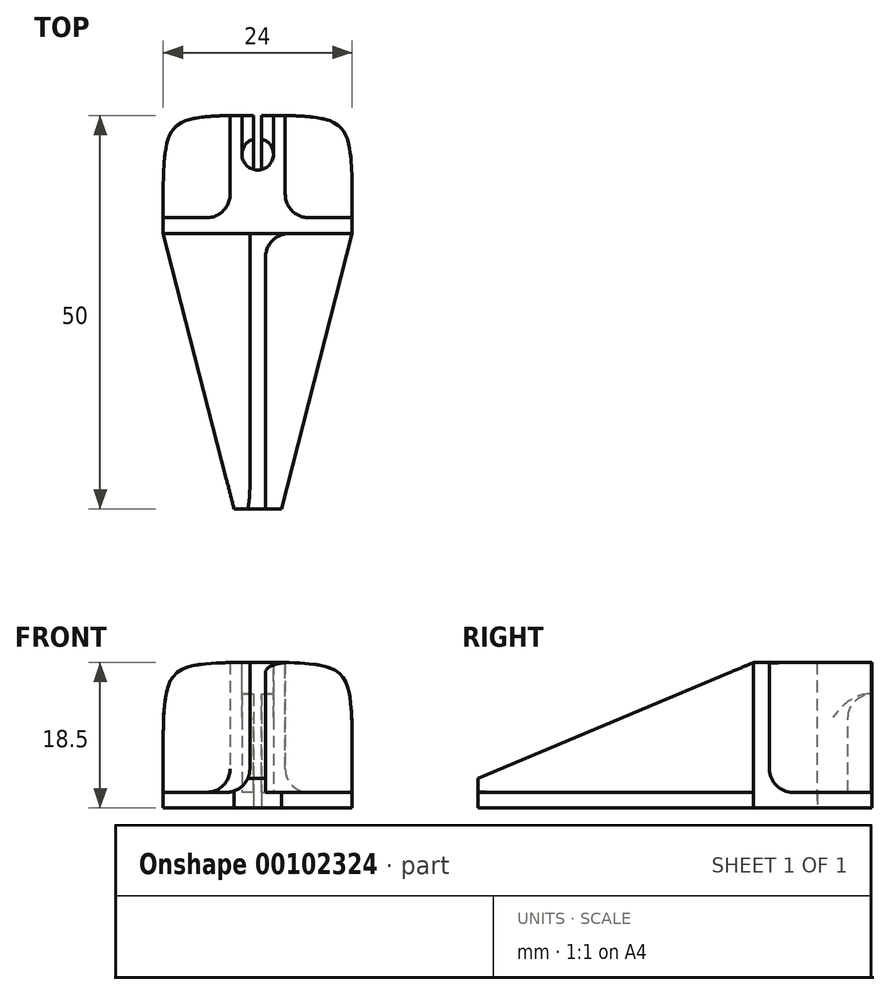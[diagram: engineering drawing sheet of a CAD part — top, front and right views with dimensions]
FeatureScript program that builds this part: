
annotation { "Feature Type Name" : "Feature", "Feature Type Description" : "" }
export const myFeature = defineFeature(function(context is Context, id is Id, definition is map)
    precondition{}
    {
        {
            var Q0;
            Q0=qCreatedBy(makeId("Top.planeOp"),FACE);
            var sketch = newSketch(context, id + "F0", { "sketchPlane" : qUnion([Q0])});
            skLineSegment(sketch, "E0", {"start": v(0.5, 1.94) * mm, "end": v(0.5, 4.94) * mm});
            skLineSegment(sketch, "E1", {"start": v(0.5, 4.94) * mm, "end": v(12, 4.94) * mm});
            skLineSegment(sketch, "E2", {"start": v(12, 4.94) * mm, "end": v(12, -10.06) * mm});
            skLineSegment(sketch, "E3", {"start": v(12, -10.06) * mm, "end": v(3, -45.06) * mm});
            skLineSegment(sketch, "E4", {"start": v(3, -45.06) * mm, "end": v(-3, -45.06) * mm});
            skLineSegment(sketch, "E5", {"start": v(-3, -45.06) * mm, "end": v(-12, -10.06) * mm});
            skLineSegment(sketch, "E6", {"start": v(-12, -10.06) * mm, "end": v(-12, 4.94) * mm});
            skLineSegment(sketch, "E7", {"start": v(-12, 4.94) * mm, "end": v(-0.5, 4.94) * mm});
            skLineSegment(sketch, "E8", {"start": v(-0.5, 4.94) * mm, "end": v(-0.5, 1.94) * mm});
            skLineSegment(sketch, "E9", {"start": v(0, 0) * mm, "end": v(0, -45.06) * mm, "construction": true});
            skCircle(sketch, "E10", {"center": v(0, 0) * mm, "radius": 2 * mm, "construction": true});
            skLineSegment(sketch, "E11", {"start": v(-0.5, 1.94) * mm, "end": v(-0.5, -1.94) * mm});
            skLineSegment(sketch, "E12", {"start": v(-0.5, -1.94) * mm, "end": v(0.5, -1.94) * mm, "construction": true});
            skLineSegment(sketch, "E13", {"start": v(0.5, -1.94) * mm, "end": v(0.5, 1.94) * mm});
            skArc(sketch, "E14", {"start": v(-0.5, -1.94) * mm, "mid": v(0, -2) * mm, "end": v(0.5, -1.94) * mm});
            skSolve(sketch);
        }
        {
            var Q0;
            Q0 = qSketchRegion(id + "F0", true);
            extrude(context, id + "F1", {"entities" : qUnion([Q0]), "depth" : 2 * mm});
        }
        {
            var Q0;
            Q0=makeQuery(id+"F1.opExtrude","CAP_FACE",FACE,{"disambiguationData":[OSD([sQuery(id+"F0.wireOp",EDGE,"E0"),sQuery(id+"F0.wireOp",EDGE,"E1"),sQuery(id+"F0.wireOp",EDGE,"E2"),sQuery(id+"F0.wireOp",EDGE,"E3"),sQuery(id+"F0.wireOp",EDGE,"E4"),sQuery(id+"F0.wireOp",EDGE,"E5"),sQuery(id+"F0.wireOp",EDGE,"E6"),sQuery(id+"F0.wireOp",EDGE,"E7"),sQuery(id+"F0.wireOp",EDGE,"E8"),sQuery(id+"F0.wireOp",EDGE,"xgoKKBLD-KgK2-QJkw-JTCZ-iVWtKJWPCulA")])],"isStart":false});
            var sketch = newSketch(context, id + "F2", { "sketchPlane" : qUnion([Q0])});
            skSolve(sketch);
        }
        {
            var Q0;
            Q0=makeQuery(id+"F2.imprint","IMPRINT",FACE,{"disambiguationData":[TD([[makeQuery(id+"F2.imprint","IMPRINT",EDGE,{"derivedFrom":makeQuery(id+"F1.opExtrude","CAP_EDGE",EDGE,{"disambiguationData":[OSD([sQuery(id+"F0.wireOp",EDGE,"E1")])],"isStart":false})}),-1.0]])]});
            var sketch = newSketch(context, id + "F3", { "sketchPlane" : qUnion([Q0])});
            skArc(sketch, "E15.0", {"start": v(-0.5, -1.94) * mm, "mid": v(0, -2) * mm, "end": v(0.5, -1.94) * mm});
            skLineSegment(sketch, "E15.1", {"start": v(0.5, -1.94) * mm, "end": v(0.5, 4.94) * mm});
            skLineSegment(sketch, "E15.2", {"start": v(-0.5, 4.94) * mm, "end": v(-0.5, -1.94) * mm});
            skLineSegment(sketch, "E16", {"start": v(-12, -10.06) * mm, "end": v(12, -10.06) * mm});
            skLineSegment(sketch, "E17", {"start": v(-0.5, 4.94) * mm, "end": v(-3.5, 4.94) * mm});
            skLineSegment(sketch, "E18", {"start": v(-3.5, 4.94) * mm, "end": v(-3.5, -8.06) * mm});
            skLineSegment(sketch, "E19", {"start": v(-3.5, -8.06) * mm, "end": v(-12, -8.06) * mm});
            skLineSegment(sketch, "E20", {"start": v(-12, -8.06) * mm, "end": v(-12, -10.06) * mm});
            skLineSegment(sketch, "E21", {"start": v(0.5, 4.94) * mm, "end": v(3.5, 4.94) * mm});
            skLineSegment(sketch, "E22", {"start": v(3.5, 4.94) * mm, "end": v(3.5, -8.06) * mm});
            skLineSegment(sketch, "E23", {"start": v(3.5, -8.06) * mm, "end": v(12, -8.06) * mm});
            skLineSegment(sketch, "E24", {"start": v(12, -8.06) * mm, "end": v(12, -10.06) * mm});
            skSolve(sketch);
        }
        {
            var Q0;
            Q0 = qSketchRegion(id + "F3", true);
            extrude(context, id + "F4", {"entities" : qUnion([Q0]), "operationType" : NewBodyOperationType.ADD, "depth" : 16.5 * mm});
        }
        {
            var Q0;
            Q0=makeQuery(id+"F4.opExtrude","CAP_FACE",FACE,{"disambiguationData":[OSD([sQuery(id+"F3.wireOp",EDGE,"E15.0"),sQuery(id+"F3.wireOp",EDGE,"E15.1"),sQuery(id+"F3.wireOp",EDGE,"E15.2"),sQuery(id+"F3.wireOp",EDGE,"E16"),sQuery(id+"F3.wireOp",EDGE,"E17"),sQuery(id+"F3.wireOp",EDGE,"E18"),sQuery(id+"F3.wireOp",EDGE,"E19"),sQuery(id+"F3.wireOp",EDGE,"E20"),sQuery(id+"F3.wireOp",EDGE,"E21"),sQuery(id+"F3.wireOp",EDGE,"E22"),sQuery(id+"F3.wireOp",EDGE,"E23"),sQuery(id+"F3.wireOp",EDGE,"E24")])],"isStart":false});
            var sketch = newSketch(context, id + "F5", { "sketchPlane" : qUnion([Q0])});
            skCircle(sketch, "E25", {"center": v(0, 0) * mm, "radius": 2 * mm});
            skSolve(sketch);
        }
        {
            var Q0;
            Q0 = qSketchRegion(id + "F5", true);
            var Q1;
            {var subQ0=sQuery(id+"F0.wireOp",EDGE,"E7");var subQ1=sQuery(id+"F0.wireOp",EDGE,"E6");Q1=makeQuery(id+"F4.boolean.opBoolean","SPLIT",FACE,{"disambiguationData":[TD([makeQuery(id+"F1.opExtrude","SWEPT_FACE",FACE,{"disambiguationData":[OSD([subQ0])]})])],"derivedFrom":makeQuery(id+"F1.opExtrude","CAP_FACE",FACE,{"disambiguationData":[OSD([sQuery(id+"F0.wireOp",EDGE,"E0"),sQuery(id+"F0.wireOp",EDGE,"E1"),sQuery(id+"F0.wireOp",EDGE,"E2"),sQuery(id+"F0.wireOp",EDGE,"E3"),sQuery(id+"F0.wireOp",EDGE,"E4"),sQuery(id+"F0.wireOp",EDGE,"E5"),subQ1,subQ0,sQuery(id+"F0.wireOp",EDGE,"E8"),sQuery(id+"F0.wireOp",EDGE,"E11"),sQuery(id+"F0.wireOp",EDGE,"E13"),sQuery(id+"F0.wireOp",EDGE,"E14")])],"isStart":false})});}
            extrude(context, id + "F6", {"entities" : qUnion([Q0]), "operationType" : NewBodyOperationType.REMOVE, "endBound" : BoundingType.UP_TO_SURFACE, "oppositeDirection" : true, "endBoundEntityFace" : qUnion([Q1]), "depth" : 25 * mm});
        }
        {
            var Q0;
            Q0=qCreatedBy(makeId("Right.planeOp"),FACE);
            var sketch = newSketch(context, id + "F7", { "sketchPlane" : qUnion([Q0])});
            skLineSegment(sketch, "E26", {"start": v(-45.06, 2) * mm, "end": v(-10.06, 2) * mm});
            skLineSegment(sketch, "E27", {"start": v(-10.06, 2) * mm, "end": v(-10.06, 18.5) * mm});
            skLineSegment(sketch, "E28", {"start": v(-10.06, 18.5) * mm, "end": v(-45.06, 3.8) * mm});
            skLineSegment(sketch, "E29", {"start": v(-45.06, 3.8) * mm, "end": v(-45.06, 2) * mm});
            skSolve(sketch);
        }
        {
            var Q0;
            Q0 = qSketchRegion(id + "F7", true);
            extrude(context, id + "F8", {"entities" : qUnion([Q0]), "operationType" : NewBodyOperationType.ADD, "endBound" : BoundingType.SYMMETRIC, "depth" : 2 * mm});
        }
        {
            var Q0;
            Q0=makeQuery(id+"F4.opExtrude","CAP_FACE",FACE,{"disambiguationData":[OSD([sQuery(id+"F3.wireOp",EDGE,"E15.0"),sQuery(id+"F3.wireOp",EDGE,"E15.1"),sQuery(id+"F3.wireOp",EDGE,"E15.2"),sQuery(id+"F3.wireOp",EDGE,"E16"),sQuery(id+"F3.wireOp",EDGE,"E17"),sQuery(id+"F3.wireOp",EDGE,"E18"),sQuery(id+"F3.wireOp",EDGE,"E19"),sQuery(id+"F3.wireOp",EDGE,"E20"),sQuery(id+"F3.wireOp",EDGE,"E21"),sQuery(id+"F3.wireOp",EDGE,"E22"),sQuery(id+"F3.wireOp",EDGE,"E23"),sQuery(id+"F3.wireOp",EDGE,"E24")])],"isStart":false});
            var sketch = newSketch(context, id + "F9", { "sketchPlane" : qUnion([Q0])});
            skLineSegment(sketch, "E30.bottom", {"start": v(-2, 4.94) * mm, "end": v(2, 4.94) * mm});
            skLineSegment(sketch, "E30.top", {"start": v(-2, 0) * mm, "end": v(2, 0) * mm});
            skLineSegment(sketch, "E30.left", {"start": v(-2, 4.94) * mm, "end": v(-2, 0) * mm});
            skLineSegment(sketch, "E30.right", {"start": v(2, 4.94) * mm, "end": v(2, 0) * mm});
            skSolve(sketch);
        }
        {
            var Q0;
            Q0 = qSketchRegion(id + "F9", true);
            extrude(context, id + "F10", {"entities" : qUnion([Q0]), "operationType" : NewBodyOperationType.REMOVE, "oppositeDirection" : true, "depth" : 4 * mm});
        }
        {
            var Q0;
            Q0=makeQuery(id+"F10.boolean.opBoolean","INTERSECT",EDGE,{"disambiguationData":[OD(1.0)],"derivedFrom":[makeQuery(id+"F6.boolean.opBoolean","MERGE",FACE,{"derivedFrom":[makeQuery(id+"F4.boolean.opBoolean","MERGE",FACE,{"derivedFrom":[makeQuery(id+"F1.opExtrude","SWEPT_FACE",FACE,{"disambiguationData":[OSD([sQuery(id+"F0.wireOp",EDGE,"E14")])]}),makeQuery(id+"F4.opExtrude","SWEPT_FACE",FACE,{"disambiguationData":[OSD([sQuery(id+"F3.wireOp",EDGE,"E15.0")])]})]}),makeQuery(id+"F6.opExtrude","SWEPT_FACE",FACE,{"disambiguationData":[OSD([sQuery(id+"F5.wireOp",EDGE,"E25")])]})]}),makeQuery(id+"F10.opExtrude","CAP_FACE",FACE,{"disambiguationData":[OSD([sQuery(id+"F9.wireOp",EDGE,"E30.bottom"),sQuery(id+"F9.wireOp",EDGE,"E30.top"),sQuery(id+"F9.wireOp",EDGE,"E30.left"),sQuery(id+"F9.wireOp",EDGE,"E30.right")])],"isStart":false})]});
            var Q1;
            Q1=makeQuery(id+"F10.boolean.opBoolean","INTERSECT",EDGE,{"disambiguationData":[OD(0.0)],"derivedFrom":[makeQuery(id+"F6.boolean.opBoolean","MERGE",FACE,{"derivedFrom":[makeQuery(id+"F4.boolean.opBoolean","MERGE",FACE,{"derivedFrom":[makeQuery(id+"F1.opExtrude","SWEPT_FACE",FACE,{"disambiguationData":[OSD([sQuery(id+"F0.wireOp",EDGE,"E14")])]}),makeQuery(id+"F4.opExtrude","SWEPT_FACE",FACE,{"disambiguationData":[OSD([sQuery(id+"F3.wireOp",EDGE,"E15.0")])]})]}),makeQuery(id+"F6.opExtrude","SWEPT_FACE",FACE,{"disambiguationData":[OSD([sQuery(id+"F5.wireOp",EDGE,"E25")])]})]}),makeQuery(id+"F10.opExtrude","CAP_FACE",FACE,{"disambiguationData":[OSD([sQuery(id+"F9.wireOp",EDGE,"E30.bottom"),sQuery(id+"F9.wireOp",EDGE,"E30.top"),sQuery(id+"F9.wireOp",EDGE,"E30.left"),sQuery(id+"F9.wireOp",EDGE,"E30.right")])],"isStart":false})]});
            fillet(context, id + "F11", {"entities" : qUnion([Q0, Q1]), "radius" : 3 * mm, "tangentPropagation" : true, "allowEdgeOverflow" : false});
        }
        {
            var Q0;
            Q0=makeQuery(id+"F4.opExtrude","CAP_EDGE",EDGE,{"disambiguationData":[OSD([sQuery(id+"F3.wireOp",EDGE,"E24")])],"isStart":false});
            var Q1;
            Q1=makeQuery(id+"F4.opExtrude","CAP_EDGE",EDGE,{"disambiguationData":[OSD([sQuery(id+"F3.wireOp",EDGE,"E20")])],"isStart":false});
            var Q2;
            Q2=makeQuery(id+"F1.opExtrude","SWEPT_EDGE",EDGE,{"disambiguationData":[OSD([sQuery(id+"F0.wireOp",EDGE,"E1"),sQuery(id+"F0.wireOp",EDGE,"E2")])]});
            var Q3;
            Q3=makeQuery(id+"F1.opExtrude","SWEPT_EDGE",EDGE,{"disambiguationData":[OSD([sQuery(id+"F0.wireOp",EDGE,"E6"),sQuery(id+"F0.wireOp",EDGE,"E7")])]});
            fillet(context, id + "F12", {"entities" : qUnion([Q0, Q1, Q2, Q3]), "radius" : 10 * mm, "tangentPropagation" : true, "rho" : .7, "crossSection" : FilletCrossSection.CONIC, "allowEdgeOverflow" : false});
        }
        {
            var Q0;
            Q0=makeQuery(id+"F8.opExtrude","CAP_EDGE",EDGE,{"disambiguationData":[OSD([sQuery(id+"F7.wireOp",EDGE,"E26")])],"isStart":true});
            var Q1;
            {var subQ0=sQuery(id+"F3.wireOp",EDGE,"E16");var subQ2=sQuery(id+"F0.wireOp",EDGE,"E5");Q1=makeQuery(id+"F8.boolean.opBoolean","SPLIT",EDGE,{"disambiguationData":[TD([makeQuery(id+"F1.opExtrude","SWEPT_FACE",FACE,{"disambiguationData":[OSD([subQ2])]})])],"derivedFrom":makeQuery(id+"F4.opExtrude","CAP_EDGE",EDGE,{"disambiguationData":[OSD([subQ0])],"isStart":true})});}
            var Q2;
            Q2=makeQuery(id+"F8.opExtrude","CAP_EDGE",EDGE,{"disambiguationData":[OSD([sQuery(id+"F7.wireOp",EDGE,"E27")])],"isStart":true});
            var Q3;
            Q3=makeQuery(id+"F8.opExtrude","CAP_EDGE",EDGE,{"disambiguationData":[OSD([sQuery(id+"F7.wireOp",EDGE,"E26")])],"isStart":false});
            var Q4;
            {var subQ0=sQuery(id+"F3.wireOp",EDGE,"E16");var subQ2=sQuery(id+"F0.wireOp",EDGE,"E2");Q4=makeQuery(id+"F8.boolean.opBoolean","SPLIT",EDGE,{"disambiguationData":[TD([makeQuery(id+"F1.opExtrude","SWEPT_FACE",FACE,{"disambiguationData":[OSD([subQ2])]})])],"derivedFrom":makeQuery(id+"F4.opExtrude","CAP_EDGE",EDGE,{"disambiguationData":[OSD([subQ0])],"isStart":true})});}
            var Q5;
            Q5=makeQuery(id+"F8.opExtrude","CAP_EDGE",EDGE,{"disambiguationData":[OSD([sQuery(id+"F7.wireOp",EDGE,"E27")])],"isStart":false});
            var Q6;
            Q6=makeQuery(id+"F4.opExtrude","CAP_EDGE",EDGE,{"disambiguationData":[OSD([sQuery(id+"F3.wireOp",EDGE,"E23")])],"isStart":true});
            var Q7;
            Q7=makeQuery(id+"F4.opExtrude","CAP_EDGE",EDGE,{"disambiguationData":[OSD([sQuery(id+"F3.wireOp",EDGE,"E22")])],"isStart":true});
            var Q8;
            Q8=makeQuery(id+"F4.opExtrude","SWEPT_EDGE",EDGE,{"disambiguationData":[OSD([sQuery(id+"F3.wireOp",EDGE,"E22"),sQuery(id+"F3.wireOp",EDGE,"E23")])]});
            var Q9;
            Q9=makeQuery(id+"F4.opExtrude","CAP_EDGE",EDGE,{"disambiguationData":[OSD([sQuery(id+"F3.wireOp",EDGE,"E18")])],"isStart":true});
            var Q10;
            Q10=makeQuery(id+"F4.opExtrude","CAP_EDGE",EDGE,{"disambiguationData":[OSD([sQuery(id+"F3.wireOp",EDGE,"E19")])],"isStart":true});
            var Q11;
            Q11=makeQuery(id+"F4.opExtrude","SWEPT_EDGE",EDGE,{"disambiguationData":[OSD([sQuery(id+"F3.wireOp",EDGE,"E18"),sQuery(id+"F3.wireOp",EDGE,"E19")])]});
            fillet(context, id + "F13", {"entities" : qUnion([Q0, Q1, Q2, Q3, Q4, Q5, Q6, Q7, Q8, Q9, Q10, Q11]), "radius" : 3 * mm, "tangentPropagation" : true, "allowEdgeOverflow" : false});
        }
    });
